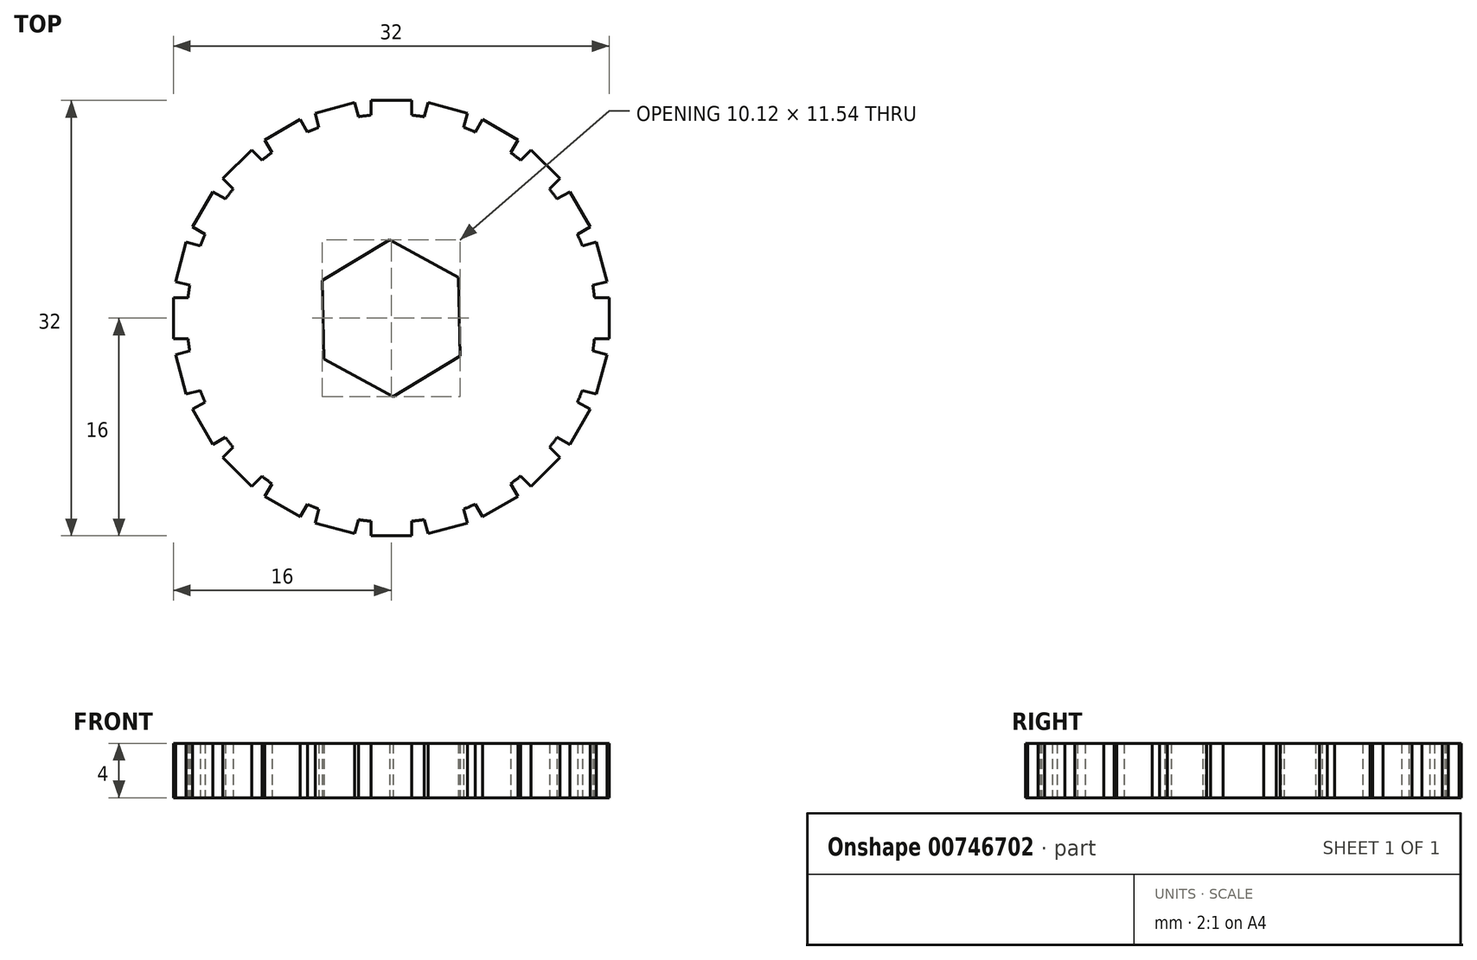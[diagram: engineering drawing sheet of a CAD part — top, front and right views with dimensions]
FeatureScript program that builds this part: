
annotation { "Feature Type Name" : "Feature", "Feature Type Description" : "" }
export const myFeature = defineFeature(function(context is Context, id is Id, definition is map)
    precondition{}
    {
        {
            var Q0;
            Q0=qCreatedBy(makeId("Top.planeOp"),FACE);
            var sketch = newSketch(context, id + "F0", { "sketchPlane" : qUnion([Q0])});
            skCircle(sketch, "E0", {"center": v(0, 0) * mm, "radius": 15 * mm});
            skCircle(sketch, "E1.cCircle", {"center": v(0, 0) * mm, "radius": 5 * mm, "construction": true});
            skLineSegment(sketch, "E1.0", {"start": v(0.12, -5.77) * mm, "end": v(-4.94, -3) * mm});
            skLineSegment(sketch, "E1.1", {"start": v(-4.94, -3) * mm, "end": v(-5.06, 2.78) * mm});
            skLineSegment(sketch, "E1.2", {"start": v(-5.06, 2.78) * mm, "end": v(-0.12, 5.77) * mm});
            skLineSegment(sketch, "E1.3", {"start": v(-0.12, 5.77) * mm, "end": v(4.94, 3) * mm});
            skLineSegment(sketch, "E1.4", {"start": v(4.94, 3) * mm, "end": v(5.06, -2.78) * mm});
            skLineSegment(sketch, "E1.5", {"start": v(5.06, -2.78) * mm, "end": v(0.12, -5.77) * mm});
            skPoint(sketch, "E1.0.midPoint", {"position": v(-2.4, -4.38) * mm});
            skLineSegment(sketch, "E2.bottom", {"start": v(-1.5, 14) * mm, "end": v(1.5, 14) * mm});
            skLineSegment(sketch, "E2.top", {"start": v(-1.5, 16) * mm, "end": v(1.5, 16) * mm});
            skLineSegment(sketch, "E2.left", {"start": v(-1.5, 14) * mm, "end": v(-1.5, 16) * mm});
            skLineSegment(sketch, "E2.right", {"start": v(1.5, 14) * mm, "end": v(1.5, 16) * mm});
            skPoint(sketch, "E2.middle", {"position": v(0, 15) * mm});
            skPoint(sketch, "E3", {"position": v(-1.5, 14.92) * mm});
            skPoint(sketch, "E4", {"position": v(1.5, 14.92) * mm});
            skLineSegment(sketch, "E5.1.0", {"start": v(2.17, 13.91) * mm, "end": v(2.7, 15.84) * mm});
            skLineSegment(sketch, "E5.1.1", {"start": v(2.7, 15.84) * mm, "end": v(5.59, 15.07) * mm});
            skLineSegment(sketch, "E5.1.2", {"start": v(5.07, 13.13) * mm, "end": v(5.59, 15.07) * mm});
            skLineSegment(sketch, "E5.1.3", {"start": v(2.17, 13.91) * mm, "end": v(5.07, 13.13) * mm});
            skLineSegment(sketch, "E5.2.0", {"start": v(5.7, 12.87) * mm, "end": v(6.7, 14.6) * mm});
            skLineSegment(sketch, "E5.2.1", {"start": v(6.7, 14.6) * mm, "end": v(9.3, 13.1) * mm});
            skLineSegment(sketch, "E5.2.2", {"start": v(8.3, 11.37) * mm, "end": v(9.3, 13.1) * mm});
            skLineSegment(sketch, "E5.2.3", {"start": v(5.7, 12.87) * mm, "end": v(8.3, 11.37) * mm});
            skLineSegment(sketch, "E5.3.0", {"start": v(8.84, 10.96) * mm, "end": v(10.25, 12.37) * mm});
            skLineSegment(sketch, "E5.3.1", {"start": v(10.25, 12.37) * mm, "end": v(12.37, 10.25) * mm});
            skLineSegment(sketch, "E5.3.2", {"start": v(10.96, 8.84) * mm, "end": v(12.37, 10.25) * mm});
            skLineSegment(sketch, "E5.3.3", {"start": v(8.84, 10.96) * mm, "end": v(10.96, 8.84) * mm});
            skLineSegment(sketch, "E5.4.0", {"start": v(11.37, 8.3) * mm, "end": v(13.1, 9.3) * mm});
            skLineSegment(sketch, "E5.4.1", {"start": v(13.1, 9.3) * mm, "end": v(14.6, 6.7) * mm});
            skLineSegment(sketch, "E5.4.2", {"start": v(12.87, 5.7) * mm, "end": v(14.6, 6.7) * mm});
            skLineSegment(sketch, "E5.4.3", {"start": v(11.37, 8.3) * mm, "end": v(12.87, 5.7) * mm});
            skLineSegment(sketch, "E5.5.0", {"start": v(13.13, 5.07) * mm, "end": v(15.07, 5.59) * mm});
            skLineSegment(sketch, "E5.5.1", {"start": v(15.07, 5.59) * mm, "end": v(15.84, 2.7) * mm});
            skLineSegment(sketch, "E5.5.2", {"start": v(13.91, 2.17) * mm, "end": v(15.84, 2.7) * mm});
            skLineSegment(sketch, "E5.5.3", {"start": v(13.13, 5.07) * mm, "end": v(13.91, 2.17) * mm});
            skLineSegment(sketch, "E5.6.0", {"start": v(14, 1.5) * mm, "end": v(16, 1.5) * mm});
            skLineSegment(sketch, "E5.6.1", {"start": v(16, 1.5) * mm, "end": v(16, -1.5) * mm});
            skLineSegment(sketch, "E5.6.2", {"start": v(14, -1.5) * mm, "end": v(16, -1.5) * mm});
            skLineSegment(sketch, "E5.6.3", {"start": v(14, 1.5) * mm, "end": v(14, -1.5) * mm});
            skLineSegment(sketch, "E5.7.0", {"start": v(13.91, -2.17) * mm, "end": v(15.84, -2.7) * mm});
            skLineSegment(sketch, "E5.7.1", {"start": v(15.84, -2.7) * mm, "end": v(15.07, -5.59) * mm});
            skLineSegment(sketch, "E5.7.2", {"start": v(13.13, -5.07) * mm, "end": v(15.07, -5.59) * mm});
            skLineSegment(sketch, "E5.7.3", {"start": v(13.91, -2.17) * mm, "end": v(13.13, -5.07) * mm});
            skLineSegment(sketch, "E5.8.0", {"start": v(12.87, -5.7) * mm, "end": v(14.6, -6.7) * mm});
            skLineSegment(sketch, "E5.8.1", {"start": v(14.6, -6.7) * mm, "end": v(13.1, -9.3) * mm});
            skLineSegment(sketch, "E5.8.2", {"start": v(11.37, -8.3) * mm, "end": v(13.1, -9.3) * mm});
            skLineSegment(sketch, "E5.8.3", {"start": v(12.87, -5.7) * mm, "end": v(11.37, -8.3) * mm});
            skLineSegment(sketch, "E5.9.0", {"start": v(10.96, -8.84) * mm, "end": v(12.37, -10.25) * mm});
            skLineSegment(sketch, "E5.9.1", {"start": v(12.37, -10.25) * mm, "end": v(10.25, -12.37) * mm});
            skLineSegment(sketch, "E5.9.2", {"start": v(8.84, -10.96) * mm, "end": v(10.25, -12.37) * mm});
            skLineSegment(sketch, "E5.9.3", {"start": v(10.96, -8.84) * mm, "end": v(8.84, -10.96) * mm});
            skLineSegment(sketch, "E5.10.0", {"start": v(8.3, -11.37) * mm, "end": v(9.3, -13.1) * mm});
            skLineSegment(sketch, "E5.10.1", {"start": v(9.3, -13.1) * mm, "end": v(6.7, -14.6) * mm});
            skLineSegment(sketch, "E5.10.2", {"start": v(5.7, -12.87) * mm, "end": v(6.7, -14.6) * mm});
            skLineSegment(sketch, "E5.10.3", {"start": v(8.3, -11.37) * mm, "end": v(5.7, -12.87) * mm});
            skLineSegment(sketch, "E5.11.0", {"start": v(5.07, -13.13) * mm, "end": v(5.59, -15.07) * mm});
            skLineSegment(sketch, "E5.11.1", {"start": v(5.59, -15.07) * mm, "end": v(2.7, -15.84) * mm});
            skLineSegment(sketch, "E5.11.2", {"start": v(2.17, -13.91) * mm, "end": v(2.7, -15.84) * mm});
            skLineSegment(sketch, "E5.11.3", {"start": v(5.07, -13.13) * mm, "end": v(2.17, -13.91) * mm});
            skLineSegment(sketch, "E5.12.0", {"start": v(1.5, -14) * mm, "end": v(1.5, -16) * mm});
            skLineSegment(sketch, "E5.12.1", {"start": v(1.5, -16) * mm, "end": v(-1.5, -16) * mm});
            skLineSegment(sketch, "E5.12.2", {"start": v(-1.5, -14) * mm, "end": v(-1.5, -16) * mm});
            skLineSegment(sketch, "E5.12.3", {"start": v(1.5, -14) * mm, "end": v(-1.5, -14) * mm});
            skLineSegment(sketch, "E5.13.0", {"start": v(-2.17, -13.91) * mm, "end": v(-2.7, -15.84) * mm});
            skLineSegment(sketch, "E5.13.1", {"start": v(-2.7, -15.84) * mm, "end": v(-5.59, -15.07) * mm});
            skLineSegment(sketch, "E5.13.2", {"start": v(-5.07, -13.13) * mm, "end": v(-5.59, -15.07) * mm});
            skLineSegment(sketch, "E5.13.3", {"start": v(-2.17, -13.91) * mm, "end": v(-5.07, -13.13) * mm});
            skLineSegment(sketch, "E5.14.0", {"start": v(-5.7, -12.87) * mm, "end": v(-6.7, -14.6) * mm});
            skLineSegment(sketch, "E5.14.1", {"start": v(-6.7, -14.6) * mm, "end": v(-9.3, -13.1) * mm});
            skLineSegment(sketch, "E5.14.2", {"start": v(-8.3, -11.37) * mm, "end": v(-9.3, -13.1) * mm});
            skLineSegment(sketch, "E5.14.3", {"start": v(-5.7, -12.87) * mm, "end": v(-8.3, -11.37) * mm});
            skLineSegment(sketch, "E5.15.0", {"start": v(-8.84, -10.96) * mm, "end": v(-10.25, -12.37) * mm});
            skLineSegment(sketch, "E5.15.1", {"start": v(-10.25, -12.37) * mm, "end": v(-12.37, -10.25) * mm});
            skLineSegment(sketch, "E5.15.2", {"start": v(-10.96, -8.84) * mm, "end": v(-12.37, -10.25) * mm});
            skLineSegment(sketch, "E5.15.3", {"start": v(-8.84, -10.96) * mm, "end": v(-10.96, -8.84) * mm});
            skLineSegment(sketch, "E5.16.0", {"start": v(-11.37, -8.3) * mm, "end": v(-13.1, -9.3) * mm});
            skLineSegment(sketch, "E5.16.1", {"start": v(-13.1, -9.3) * mm, "end": v(-14.6, -6.7) * mm});
            skLineSegment(sketch, "E5.16.2", {"start": v(-12.87, -5.7) * mm, "end": v(-14.6, -6.7) * mm});
            skLineSegment(sketch, "E5.16.3", {"start": v(-11.37, -8.3) * mm, "end": v(-12.87, -5.7) * mm});
            skLineSegment(sketch, "E5.17.0", {"start": v(-13.13, -5.07) * mm, "end": v(-15.07, -5.59) * mm});
            skLineSegment(sketch, "E5.17.1", {"start": v(-15.07, -5.59) * mm, "end": v(-15.84, -2.7) * mm});
            skLineSegment(sketch, "E5.17.2", {"start": v(-13.91, -2.17) * mm, "end": v(-15.84, -2.7) * mm});
            skLineSegment(sketch, "E5.17.3", {"start": v(-13.13, -5.07) * mm, "end": v(-13.91, -2.17) * mm});
            skLineSegment(sketch, "E5.18.0", {"start": v(-14, -1.5) * mm, "end": v(-16, -1.5) * mm});
            skLineSegment(sketch, "E5.18.1", {"start": v(-16, -1.5) * mm, "end": v(-16, 1.5) * mm});
            skLineSegment(sketch, "E5.18.2", {"start": v(-14, 1.5) * mm, "end": v(-16, 1.5) * mm});
            skLineSegment(sketch, "E5.18.3", {"start": v(-14, -1.5) * mm, "end": v(-14, 1.5) * mm});
            skLineSegment(sketch, "E5.19.0", {"start": v(-13.91, 2.17) * mm, "end": v(-15.84, 2.7) * mm});
            skLineSegment(sketch, "E5.19.1", {"start": v(-15.84, 2.7) * mm, "end": v(-15.07, 5.59) * mm});
            skLineSegment(sketch, "E5.19.2", {"start": v(-13.13, 5.07) * mm, "end": v(-15.07, 5.59) * mm});
            skLineSegment(sketch, "E5.19.3", {"start": v(-13.91, 2.17) * mm, "end": v(-13.13, 5.07) * mm});
            skLineSegment(sketch, "E5.20.0", {"start": v(-12.87, 5.7) * mm, "end": v(-14.6, 6.7) * mm});
            skLineSegment(sketch, "E5.20.1", {"start": v(-14.6, 6.7) * mm, "end": v(-13.1, 9.3) * mm});
            skLineSegment(sketch, "E5.20.2", {"start": v(-11.37, 8.3) * mm, "end": v(-13.1, 9.3) * mm});
            skLineSegment(sketch, "E5.20.3", {"start": v(-12.87, 5.7) * mm, "end": v(-11.37, 8.3) * mm});
            skLineSegment(sketch, "E5.21.0", {"start": v(-10.96, 8.84) * mm, "end": v(-12.37, 10.25) * mm});
            skLineSegment(sketch, "E5.21.1", {"start": v(-12.37, 10.25) * mm, "end": v(-10.25, 12.37) * mm});
            skLineSegment(sketch, "E5.21.2", {"start": v(-8.84, 10.96) * mm, "end": v(-10.25, 12.37) * mm});
            skLineSegment(sketch, "E5.21.3", {"start": v(-10.96, 8.84) * mm, "end": v(-8.84, 10.96) * mm});
            skLineSegment(sketch, "E5.22.0", {"start": v(-8.3, 11.37) * mm, "end": v(-9.3, 13.1) * mm});
            skLineSegment(sketch, "E5.22.1", {"start": v(-9.3, 13.1) * mm, "end": v(-6.7, 14.6) * mm});
            skLineSegment(sketch, "E5.22.2", {"start": v(-5.7, 12.87) * mm, "end": v(-6.7, 14.6) * mm});
            skLineSegment(sketch, "E5.22.3", {"start": v(-8.3, 11.37) * mm, "end": v(-5.7, 12.87) * mm});
            skLineSegment(sketch, "E5.23.0", {"start": v(-5.07, 13.13) * mm, "end": v(-5.59, 15.07) * mm});
            skLineSegment(sketch, "E5.23.1", {"start": v(-5.59, 15.07) * mm, "end": v(-2.7, 15.84) * mm});
            skLineSegment(sketch, "E5.23.2", {"start": v(-2.17, 13.91) * mm, "end": v(-2.7, 15.84) * mm});
            skLineSegment(sketch, "E5.23.3", {"start": v(-5.07, 13.13) * mm, "end": v(-2.17, 13.91) * mm});
            skLineSegment(sketch, "E5.anchor1", {"start": v(0, 0) * mm, "end": v(-1.5, 14) * mm, "construction": true});
            skLineSegment(sketch, "E5.anchor2", {"start": v(0, 0) * mm, "end": v(-5.07, 13.13) * mm, "construction": true});
            skSolve(sketch);
        }
        {
            var Q0;
            {var subQ5=sQuery(id+"F0.wireOp",EDGE,"E5.17.3");Q0=makeQuery(id+"F0.imprint","IMPRINT",FACE,{"disambiguationData":[TD([[makeQuery(id+"F0.imprint","IMPRINT",EDGE,{"derivedFrom":subQ5}),1.0]])]});}
            var Q1;
            {var subQ5=sQuery(id+"F0.wireOp",EDGE,"E5.15.1");Q1=makeQuery(id+"F0.imprint","IMPRINT",FACE,{"disambiguationData":[TD([[makeQuery(id+"F0.imprint","IMPRINT",EDGE,{"derivedFrom":subQ5}),-1.0]])]});}
            var Q2;
            {var subQ5=sQuery(id+"F0.wireOp",EDGE,"E5.8.1");Q2=makeQuery(id+"F0.imprint","IMPRINT",FACE,{"disambiguationData":[TD([[makeQuery(id+"F0.imprint","IMPRINT",EDGE,{"derivedFrom":subQ5}),-1.0]])]});}
            var Q3;
            {var subQ5=sQuery(id+"F0.wireOp",EDGE,"E5.18.3");Q3=makeQuery(id+"F0.imprint","IMPRINT",FACE,{"disambiguationData":[TD([[makeQuery(id+"F0.imprint","IMPRINT",EDGE,{"derivedFrom":subQ5}),1.0]])]});}
            var Q4;
            {var subQ5=sQuery(id+"F0.wireOp",EDGE,"E5.9.1");Q4=makeQuery(id+"F0.imprint","IMPRINT",FACE,{"disambiguationData":[TD([[makeQuery(id+"F0.imprint","IMPRINT",EDGE,{"derivedFrom":subQ5}),-1.0]])]});}
            var Q5;
            {var subQ5=sQuery(id+"F0.wireOp",EDGE,"E5.19.3");Q5=makeQuery(id+"F0.imprint","IMPRINT",FACE,{"disambiguationData":[TD([[makeQuery(id+"F0.imprint","IMPRINT",EDGE,{"derivedFrom":subQ5}),1.0]])]});}
            var Q6;
            {var subQ5=sQuery(id+"F0.wireOp",EDGE,"E5.16.1");Q6=makeQuery(id+"F0.imprint","IMPRINT",FACE,{"disambiguationData":[TD([[makeQuery(id+"F0.imprint","IMPRINT",EDGE,{"derivedFrom":subQ5}),-1.0]])]});}
            var Q7;
            {var subQ5=sQuery(id+"F0.wireOp",EDGE,"E5.10.1");Q7=makeQuery(id+"F0.imprint","IMPRINT",FACE,{"disambiguationData":[TD([[makeQuery(id+"F0.imprint","IMPRINT",EDGE,{"derivedFrom":subQ5}),-1.0]])]});}
            var Q8;
            {var subQ5=sQuery(id+"F0.wireOp",EDGE,"E5.20.3");Q8=makeQuery(id+"F0.imprint","IMPRINT",FACE,{"disambiguationData":[TD([[makeQuery(id+"F0.imprint","IMPRINT",EDGE,{"derivedFrom":subQ5}),1.0]])]});}
            var Q9;
            {var subQ5=sQuery(id+"F0.wireOp",EDGE,"E5.11.1");Q9=makeQuery(id+"F0.imprint","IMPRINT",FACE,{"disambiguationData":[TD([[makeQuery(id+"F0.imprint","IMPRINT",EDGE,{"derivedFrom":subQ5}),-1.0]])]});}
            var Q10;
            {var subQ5=sQuery(id+"F0.wireOp",EDGE,"E5.21.3");Q10=makeQuery(id+"F0.imprint","IMPRINT",FACE,{"disambiguationData":[TD([[makeQuery(id+"F0.imprint","IMPRINT",EDGE,{"derivedFrom":subQ5}),1.0]])]});}
            var Q11;
            Q11=makeQuery(id+"F0.imprint","IMPRINT",FACE,{"disambiguationData":[TD([[makeQuery(id+"F0.imprint","IMPRINT",EDGE,{"derivedFrom":sQuery(id+"F0.wireOp",EDGE,"E1.0")}),1.0]])]});
            var Q12;
            {var subQ5=sQuery(id+"F0.wireOp",EDGE,"E5.12.1");Q12=makeQuery(id+"F0.imprint","IMPRINT",FACE,{"disambiguationData":[TD([[makeQuery(id+"F0.imprint","IMPRINT",EDGE,{"derivedFrom":subQ5}),-1.0]])]});}
            var Q13;
            {var subQ5=sQuery(id+"F0.wireOp",EDGE,"E5.14.1");Q13=makeQuery(id+"F0.imprint","IMPRINT",FACE,{"disambiguationData":[TD([[makeQuery(id+"F0.imprint","IMPRINT",EDGE,{"derivedFrom":subQ5}),-1.0]])]});}
            var Q14;
            {var subQ5=sQuery(id+"F0.wireOp",EDGE,"E5.7.1");Q14=makeQuery(id+"F0.imprint","IMPRINT",FACE,{"disambiguationData":[TD([[makeQuery(id+"F0.imprint","IMPRINT",EDGE,{"derivedFrom":subQ5}),-1.0]])]});}
            var Q15;
            {var subQ5=sQuery(id+"F0.wireOp",EDGE,"E5.16.3");Q15=makeQuery(id+"F0.imprint","IMPRINT",FACE,{"disambiguationData":[TD([[makeQuery(id+"F0.imprint","IMPRINT",EDGE,{"derivedFrom":subQ5}),1.0]])]});}
            var Q16;
            {var subQ5=sQuery(id+"F0.wireOp",EDGE,"E5.22.3");Q16=makeQuery(id+"F0.imprint","IMPRINT",FACE,{"disambiguationData":[TD([[makeQuery(id+"F0.imprint","IMPRINT",EDGE,{"derivedFrom":subQ5}),1.0]])]});}
            var Q17;
            {var subQ5=sQuery(id+"F0.wireOp",EDGE,"E5.6.3");Q17=makeQuery(id+"F0.imprint","IMPRINT",FACE,{"disambiguationData":[TD([[makeQuery(id+"F0.imprint","IMPRINT",EDGE,{"derivedFrom":subQ5}),1.0]])]});}
            var Q18;
            {var subQ5=sQuery(id+"F0.wireOp",EDGE,"E5.13.1");Q18=makeQuery(id+"F0.imprint","IMPRINT",FACE,{"disambiguationData":[TD([[makeQuery(id+"F0.imprint","IMPRINT",EDGE,{"derivedFrom":subQ5}),-1.0]])]});}
            var Q19;
            {var subQ5=sQuery(id+"F0.wireOp",EDGE,"E5.2.3");Q19=makeQuery(id+"F0.imprint","IMPRINT",FACE,{"disambiguationData":[TD([[makeQuery(id+"F0.imprint","IMPRINT",EDGE,{"derivedFrom":subQ5}),1.0]])]});}
            var Q20;
            {var subQ5=sQuery(id+"F0.wireOp",EDGE,"E5.10.3");Q20=makeQuery(id+"F0.imprint","IMPRINT",FACE,{"disambiguationData":[TD([[makeQuery(id+"F0.imprint","IMPRINT",EDGE,{"derivedFrom":subQ5}),1.0]])]});}
            var Q21;
            {var subQ5=sQuery(id+"F0.wireOp",EDGE,"E5.8.3");Q21=makeQuery(id+"F0.imprint","IMPRINT",FACE,{"disambiguationData":[TD([[makeQuery(id+"F0.imprint","IMPRINT",EDGE,{"derivedFrom":subQ5}),1.0]])]});}
            var Q22;
            {var subQ5=sQuery(id+"F0.wireOp",EDGE,"E5.11.3");Q22=makeQuery(id+"F0.imprint","IMPRINT",FACE,{"disambiguationData":[TD([[makeQuery(id+"F0.imprint","IMPRINT",EDGE,{"derivedFrom":subQ5}),1.0]])]});}
            var Q23;
            {var subQ5=sQuery(id+"F0.wireOp",EDGE,"E5.12.3");Q23=makeQuery(id+"F0.imprint","IMPRINT",FACE,{"disambiguationData":[TD([[makeQuery(id+"F0.imprint","IMPRINT",EDGE,{"derivedFrom":subQ5}),1.0]])]});}
            var Q24;
            {var subQ5=sQuery(id+"F0.wireOp",EDGE,"E5.4.3");Q24=makeQuery(id+"F0.imprint","IMPRINT",FACE,{"disambiguationData":[TD([[makeQuery(id+"F0.imprint","IMPRINT",EDGE,{"derivedFrom":subQ5}),1.0]])]});}
            var Q25;
            {var subQ5=sQuery(id+"F0.wireOp",EDGE,"E5.3.3");Q25=makeQuery(id+"F0.imprint","IMPRINT",FACE,{"disambiguationData":[TD([[makeQuery(id+"F0.imprint","IMPRINT",EDGE,{"derivedFrom":subQ5}),1.0]])]});}
            var Q26;
            {var subQ5=sQuery(id+"F0.wireOp",EDGE,"E5.9.3");Q26=makeQuery(id+"F0.imprint","IMPRINT",FACE,{"disambiguationData":[TD([[makeQuery(id+"F0.imprint","IMPRINT",EDGE,{"derivedFrom":subQ5}),1.0]])]});}
            var Q27;
            {var subQ5=sQuery(id+"F0.wireOp",EDGE,"E5.1.3");Q27=makeQuery(id+"F0.imprint","IMPRINT",FACE,{"disambiguationData":[TD([[makeQuery(id+"F0.imprint","IMPRINT",EDGE,{"derivedFrom":subQ5}),1.0]])]});}
            var Q28;
            {var subQ5=sQuery(id+"F0.wireOp",EDGE,"E5.5.1");Q28=makeQuery(id+"F0.imprint","IMPRINT",FACE,{"disambiguationData":[TD([[makeQuery(id+"F0.imprint","IMPRINT",EDGE,{"derivedFrom":subQ5}),-1.0]])]});}
            var Q29;
            {var subQ5=sQuery(id+"F0.wireOp",EDGE,"E5.4.1");Q29=makeQuery(id+"F0.imprint","IMPRINT",FACE,{"disambiguationData":[TD([[makeQuery(id+"F0.imprint","IMPRINT",EDGE,{"derivedFrom":subQ5}),-1.0]])]});}
            var Q30;
            {var subQ5=sQuery(id+"F0.wireOp",EDGE,"E5.3.1");Q30=makeQuery(id+"F0.imprint","IMPRINT",FACE,{"disambiguationData":[TD([[makeQuery(id+"F0.imprint","IMPRINT",EDGE,{"derivedFrom":subQ5}),-1.0]])]});}
            var Q31;
            {var subQ5=sQuery(id+"F0.wireOp",EDGE,"E5.2.1");Q31=makeQuery(id+"F0.imprint","IMPRINT",FACE,{"disambiguationData":[TD([[makeQuery(id+"F0.imprint","IMPRINT",EDGE,{"derivedFrom":subQ5}),-1.0]])]});}
            var Q32;
            {var subQ5=sQuery(id+"F0.wireOp",EDGE,"E5.1.1");Q32=makeQuery(id+"F0.imprint","IMPRINT",FACE,{"disambiguationData":[TD([[makeQuery(id+"F0.imprint","IMPRINT",EDGE,{"derivedFrom":subQ5}),-1.0]])]});}
            var Q33;
            {var subQ5=sQuery(id+"F0.wireOp",EDGE,"E5.23.1");Q33=makeQuery(id+"F0.imprint","IMPRINT",FACE,{"disambiguationData":[TD([[makeQuery(id+"F0.imprint","IMPRINT",EDGE,{"derivedFrom":subQ5}),-1.0]])]});}
            var Q34;
            {var subQ5=sQuery(id+"F0.wireOp",EDGE,"E5.22.1");Q34=makeQuery(id+"F0.imprint","IMPRINT",FACE,{"disambiguationData":[TD([[makeQuery(id+"F0.imprint","IMPRINT",EDGE,{"derivedFrom":subQ5}),-1.0]])]});}
            var Q35;
            {var subQ5=sQuery(id+"F0.wireOp",EDGE,"E5.21.1");Q35=makeQuery(id+"F0.imprint","IMPRINT",FACE,{"disambiguationData":[TD([[makeQuery(id+"F0.imprint","IMPRINT",EDGE,{"derivedFrom":subQ5}),-1.0]])]});}
            var Q36;
            {var subQ5=sQuery(id+"F0.wireOp",EDGE,"E5.20.1");Q36=makeQuery(id+"F0.imprint","IMPRINT",FACE,{"disambiguationData":[TD([[makeQuery(id+"F0.imprint","IMPRINT",EDGE,{"derivedFrom":subQ5}),-1.0]])]});}
            var Q37;
            {var subQ5=sQuery(id+"F0.wireOp",EDGE,"E5.19.1");Q37=makeQuery(id+"F0.imprint","IMPRINT",FACE,{"disambiguationData":[TD([[makeQuery(id+"F0.imprint","IMPRINT",EDGE,{"derivedFrom":subQ5}),-1.0]])]});}
            var Q38;
            {var subQ5=sQuery(id+"F0.wireOp",EDGE,"E5.18.1");Q38=makeQuery(id+"F0.imprint","IMPRINT",FACE,{"disambiguationData":[TD([[makeQuery(id+"F0.imprint","IMPRINT",EDGE,{"derivedFrom":subQ5}),-1.0]])]});}
            var Q39;
            {var subQ5=sQuery(id+"F0.wireOp",EDGE,"E5.17.1");Q39=makeQuery(id+"F0.imprint","IMPRINT",FACE,{"disambiguationData":[TD([[makeQuery(id+"F0.imprint","IMPRINT",EDGE,{"derivedFrom":subQ5}),-1.0]])]});}
            var Q40;
            {var subQ5=sQuery(id+"F0.wireOp",EDGE,"E5.15.3");Q40=makeQuery(id+"F0.imprint","IMPRINT",FACE,{"disambiguationData":[TD([[makeQuery(id+"F0.imprint","IMPRINT",EDGE,{"derivedFrom":subQ5}),1.0]])]});}
            var Q41;
            {var subQ5=sQuery(id+"F0.wireOp",EDGE,"E5.6.1");Q41=makeQuery(id+"F0.imprint","IMPRINT",FACE,{"disambiguationData":[TD([[makeQuery(id+"F0.imprint","IMPRINT",EDGE,{"derivedFrom":subQ5}),-1.0]])]});}
            var Q42;
            {var subQ5=sQuery(id+"F0.wireOp",EDGE,"E5.14.3");Q42=makeQuery(id+"F0.imprint","IMPRINT",FACE,{"disambiguationData":[TD([[makeQuery(id+"F0.imprint","IMPRINT",EDGE,{"derivedFrom":subQ5}),1.0]])]});}
            var Q43;
            {var subQ5=sQuery(id+"F0.wireOp",EDGE,"E5.23.3");Q43=makeQuery(id+"F0.imprint","IMPRINT",FACE,{"disambiguationData":[TD([[makeQuery(id+"F0.imprint","IMPRINT",EDGE,{"derivedFrom":subQ5}),1.0]])]});}
            var Q44;
            {var subQ5=sQuery(id+"F0.wireOp",EDGE,"E5.13.3");Q44=makeQuery(id+"F0.imprint","IMPRINT",FACE,{"disambiguationData":[TD([[makeQuery(id+"F0.imprint","IMPRINT",EDGE,{"derivedFrom":subQ5}),1.0]])]});}
            var Q45;
            {var subQ5=sQuery(id+"F0.wireOp",EDGE,"E5.5.3");Q45=makeQuery(id+"F0.imprint","IMPRINT",FACE,{"disambiguationData":[TD([[makeQuery(id+"F0.imprint","IMPRINT",EDGE,{"derivedFrom":subQ5}),1.0]])]});}
            var Q46;
            {var subQ5=sQuery(id+"F0.wireOp",EDGE,"E5.7.3");Q46=makeQuery(id+"F0.imprint","IMPRINT",FACE,{"disambiguationData":[TD([[makeQuery(id+"F0.imprint","IMPRINT",EDGE,{"derivedFrom":subQ5}),1.0]])]});}
            var Q47;
            {var subQ5=sQuery(id+"F0.wireOp",EDGE,"E2.bottom");Q47=makeQuery(id+"F0.imprint","IMPRINT",FACE,{"disambiguationData":[TD([[makeQuery(id+"F0.imprint","IMPRINT",EDGE,{"derivedFrom":subQ5}),1.0]])]});}
            var Q48;
            {var subQ5=sQuery(id+"F0.wireOp",EDGE,"E2.top");Q48=makeQuery(id+"F0.imprint","IMPRINT",FACE,{"disambiguationData":[TD([[makeQuery(id+"F0.imprint","IMPRINT",EDGE,{"derivedFrom":subQ5}),-1.0]])]});}
            extrude(context, id + "F1", {"entities" : qUnion([Q0, Q1, Q2, Q3, Q4, Q5, Q6, Q7, Q8, Q9, Q10, Q11, Q12, Q13, Q14, Q15, Q16, Q17, Q18, Q19, Q20, Q21, Q22, Q23, Q24, Q25, Q26, Q27, Q28, Q29, Q30, Q31, Q32, Q33, Q34, Q35, Q36, Q37, Q38, Q39, Q40, Q41, Q42, Q43, Q44, Q45, Q46, Q47, Q48]), "depth" : 4 * mm, "offsetDistance" : 25 * mm});
        }
    });
